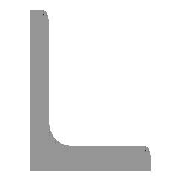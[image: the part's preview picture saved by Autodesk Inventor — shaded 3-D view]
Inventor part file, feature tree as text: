
AUTODESK INVENTOR PART (.ipt)
format: ipt  version: 2022 (Build 260153000, 153)  size: 248,320 bytes
history: native  units: mm (DEFAULTED — no unit token found)
features: other x7, sketch x3, surface_op x2, plane x1
ambient origin geometry x8: Origin, YZ Plane, XZ Plane, XY Plane, X Axis, Y Axis, Z Axis, Center Point
bodies: Solid1 (feature_tree), Body (feature_tree), Solid3 (feature_tree)
feature tree (13):
  parser-record x1  (decoder bookkeeping rows leaked as tree rows — omitted from the tree; the rows remain in map.json)
  other  "Driven Length"
  other  "Start Plane"
  other  "End Plane"
  sketch  "Sketch"  dims[d5=50.0mm d6=30.0mm d7=4.0mm d8=3.0mm d9=4.0mm d10=3.0mm d11=140.857864mm d12=0.0mm d17=5.0mm d18=2.5mm d19=8.3mm d20=8.3mm d21=-0.0mm d22=180.0mm d23=90.0deg d24=180.0mm d43=5.0mm d44=5.0mm d45=5.0mm d46=5.0mm d47=5.0mm d48=5.0mm d49=5.0mm d50=5.0mm d51=0.0mm d52=5.0mm d53=5.0mm d54=5.0mm d55=5.0mm d56=5.0mm d57=5.0mm d58=5.0mm d59=5.0mm d60=0.0mm]
  sketch  "Sketch3"  dims[d3=50.0mm]
  plane  "Work Plane10"
  sketch  "Sketch4"  dims[d4=30.0mm]
  other  "Srf5"
  other  "Srf6"
  other  "Srf4"
  surface_op  "Boundary Patch3"
  surface_op  "Boundary Patch4"
